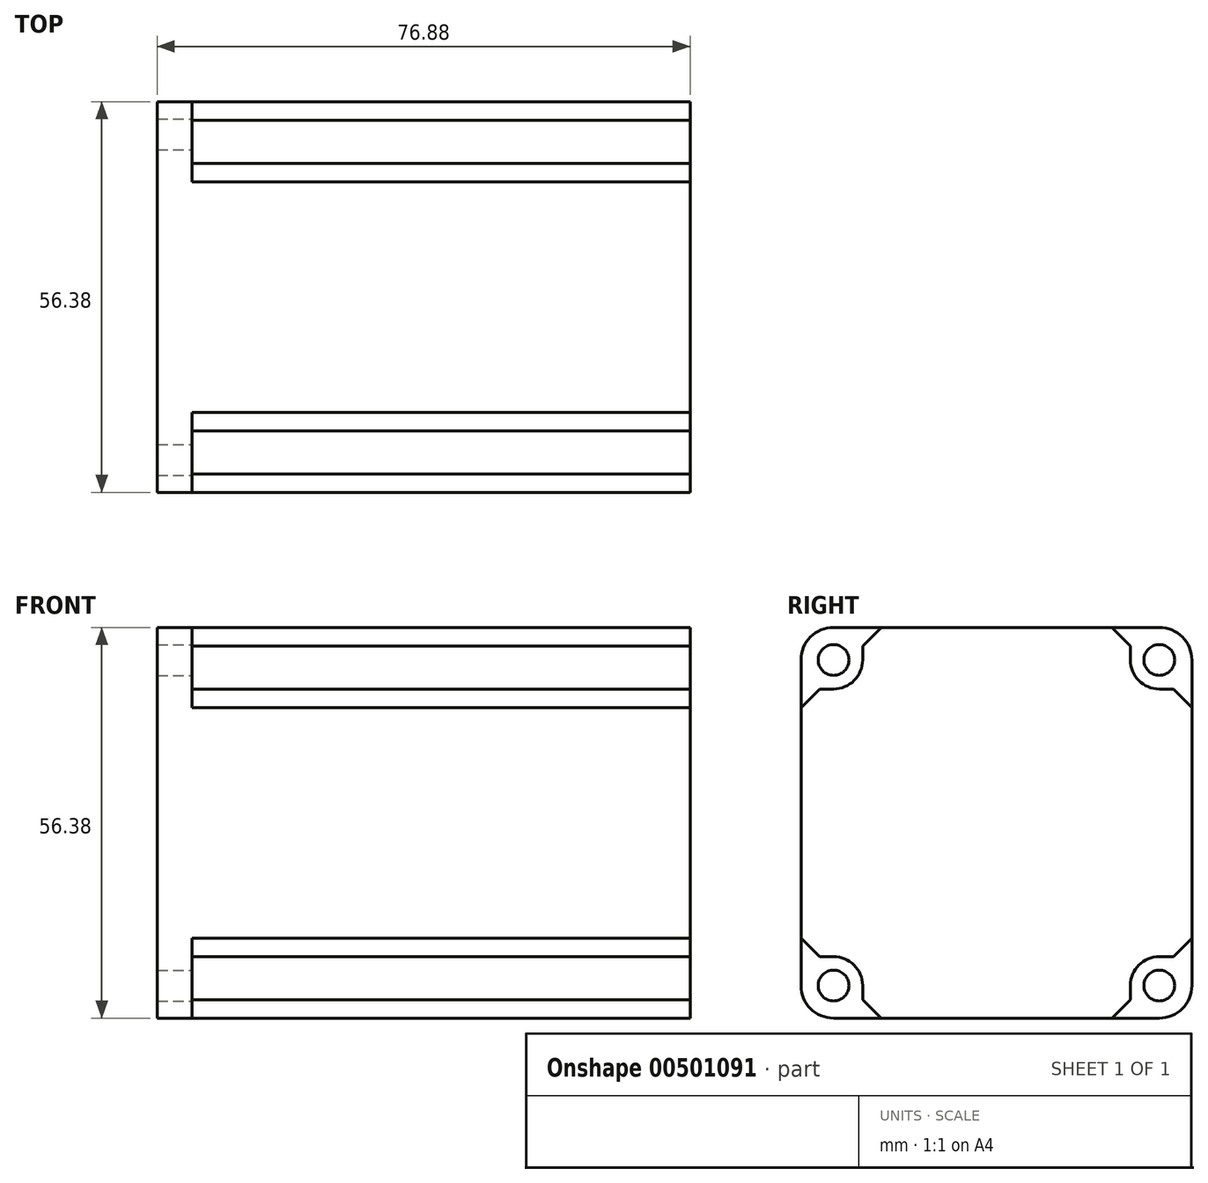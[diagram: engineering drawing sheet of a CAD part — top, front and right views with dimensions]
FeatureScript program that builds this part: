
annotation { "Feature Type Name" : "Feature", "Feature Type Description" : "" }
export const myFeature = defineFeature(function(context is Context, id is Id, definition is map)
    precondition{}
    {
        {
            var Q0;
            Q0=qCreatedBy(makeId("Right.planeOp"),FACE);
            var sketch = newSketch(context, id + "F0", { "sketchPlane" : qUnion([Q0])});
            skPoint(sketch, "E0.middle", {"position": v(0, 0) * mm});
            skLineSegment(sketch, "E1", {"start": v(-25.53, 19.3) * mm, "end": v(-23.5, 19.3) * mm});
            skLineSegment(sketch, "E2", {"start": v(-19.3, 23.5) * mm, "end": v(-19.3, 25.53) * mm});
            skCircle(sketch, "E3", {"center": v(-23.5, 23.5) * mm, "radius": 2.22 * mm});
            skArc(sketch, "E4.filletArc", {"start": v(-23.5, 28.2) * mm, "mid": v(-26.82, 26.82) * mm, "end": v(-28.2, 23.5) * mm});
            skCircle(sketch, "E5.1.1", {"center": v(-23.5, -23.5) * mm, "radius": 2.22 * mm});
            skArc(sketch, "E5.1.2", {"start": v(-28.2, -23.5) * mm, "mid": v(-26.82, -26.82) * mm, "end": v(-23.5, -28.2) * mm});
            skCircle(sketch, "E5.2.1", {"center": v(23.5, -23.5) * mm, "radius": 2.22 * mm});
            skLineSegment(sketch, "E5.2.3", {"start": v(25.53, -19.3) * mm, "end": v(23.5, -19.3) * mm});
            skLineSegment(sketch, "E5.2.4", {"start": v(19.3, -23.5) * mm, "end": v(19.3, -25.53) * mm});
            skCircle(sketch, "E5.3.1", {"center": v(23.5, 23.5) * mm, "radius": 2.22 * mm});
            skArc(sketch, "E5.3.2", {"start": v(28.2, 23.5) * mm, "mid": v(26.82, 26.82) * mm, "end": v(23.5, 28.2) * mm});
            skLineSegment(sketch, "E5.3.3", {"start": v(19.3, 25.53) * mm, "end": v(19.3, 23.5) * mm});
            skLineSegment(sketch, "E5.3.4", {"start": v(23.5, 19.3) * mm, "end": v(25.53, 19.3) * mm});
            skLineSegment(sketch, "E6", {"start": v(23.5, 28.2) * mm, "end": v(-23.5, 28.2) * mm});
            skLineSegment(sketch, "E7", {"start": v(-28.2, 23.5) * mm, "end": v(-28.2, -23.5) * mm});
            skLineSegment(sketch, "E8", {"start": v(-23.5, -28.2) * mm, "end": v(23.5, -28.2) * mm});
            skLineSegment(sketch, "E9", {"start": v(28.2, -23.5) * mm, "end": v(28.2, 23.5) * mm});
            skLineSegment(sketch, "E10", {"start": v(-28.2, 23.5) * mm, "end": v(-23.5, 23.5) * mm, "construction": true});
            skLineSegment(sketch, "E11", {"start": v(-23.5, 28.2) * mm, "end": v(-23.5, 23.5) * mm, "construction": true});
            skArc(sketch, "E12", {"start": v(23.5, -28.2) * mm, "mid": v(26.82, -26.82) * mm, "end": v(28.2, -23.5) * mm});
            skPoint(sketch, "E13.visualSharp", {"position": v(-19.3, 19.3) * mm});
            skArc(sketch, "E13.filletArc", {"start": v(-23.5, 19.3) * mm, "mid": v(-20.53, 20.53) * mm, "end": v(-19.3, 23.5) * mm});
            skPoint(sketch, "E14.visualSharp", {"position": v(19.3, 19.3) * mm});
            skPoint(sketch, "E15.visualSharp", {"position": v(19.3, -19.3) * mm});
            skArc(sketch, "E15.filletArc", {"start": v(23.5, -19.3) * mm, "mid": v(20.53, -20.53) * mm, "end": v(19.3, -23.5) * mm});
            skLineSegment(sketch, "E16", {"start": v(-23.5, -23.5) * mm, "end": v(23.5, 23.5) * mm, "construction": true});
            skLineSegment(sketch, "E17", {"start": v(-19.3, -25.53) * mm, "end": v(-19.3, -23.5) * mm});
            skLineSegment(sketch, "E18", {"start": v(-23.5, -19.3) * mm, "end": v(-25.53, -19.3) * mm});
            skArc(sketch, "E19", {"start": v(-19.3, -23.5) * mm, "mid": v(-20.53, -20.53) * mm, "end": v(-23.5, -19.3) * mm});
            skLineSegment(sketch, "E20", {"start": v(-28.2, 16.64) * mm, "end": v(-25.53, 19.3) * mm});
            skLineSegment(sketch, "E21.trimOffspring", {"start": v(-19.3, 25.53) * mm, "end": v(-16.64, 28.2) * mm});
            skLineSegment(sketch, "E22.1.0", {"start": v(-16.64, -28.2) * mm, "end": v(-19.3, -25.53) * mm});
            skLineSegment(sketch, "E22.1.1", {"start": v(-25.53, -19.3) * mm, "end": v(-28.2, -16.64) * mm});
            skLineSegment(sketch, "E22.2.0", {"start": v(28.2, -16.64) * mm, "end": v(25.53, -19.3) * mm});
            skLineSegment(sketch, "E22.2.1", {"start": v(19.3, -25.53) * mm, "end": v(16.64, -28.2) * mm});
            skLineSegment(sketch, "E22.3.0", {"start": v(16.64, 28.2) * mm, "end": v(19.3, 25.53) * mm});
            skLineSegment(sketch, "E22.3.1", {"start": v(25.53, 19.3) * mm, "end": v(28.2, 16.64) * mm});
            skArc(sketch, "E23", {"start": v(19.3, 23.5) * mm, "mid": v(20.53, 20.53) * mm, "end": v(23.5, 19.3) * mm});
            skSolve(sketch);
        }
        {
            var Q0;
            Q0=makeQuery(id+"F0.imprint","IMPRINT",FACE,{"disambiguationData":[TD([[makeQuery(id+"F0.imprint","IMPRINT",EDGE,{"derivedFrom":sQuery(id+"F0.wireOp",EDGE,"E1")}),-1.0]])]});
            extrude(context, id + "F1", {"entities" : qUnion([Q0]), "depth" : 71.88 * mm});
        }
        {
            var Q0;
            Q0 = qSketchRegion(id + "F0", true);
            extrude(context, id + "F2", {"entities" : qUnion([Q0]), "operationType" : NewBodyOperationType.ADD, "oppositeDirection" : true, "depth" : 5 * mm});
        }
    });
